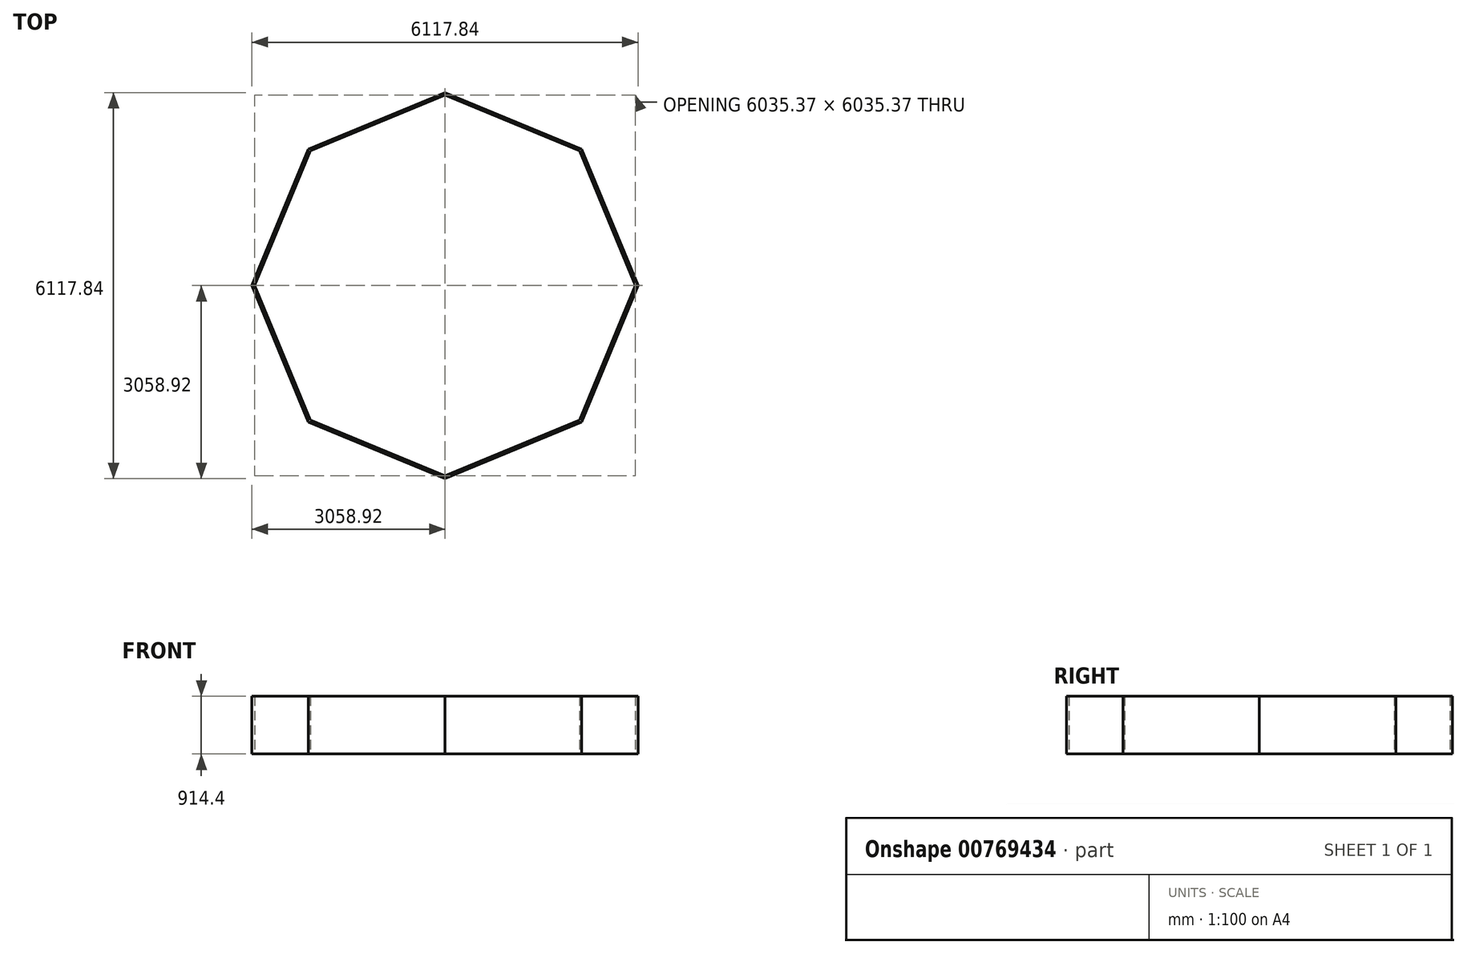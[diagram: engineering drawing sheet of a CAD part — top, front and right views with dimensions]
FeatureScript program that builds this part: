
annotation { "Feature Type Name" : "Feature", "Feature Type Description" : "" }
export const myFeature = defineFeature(function(context is Context, id is Id, definition is map)
    precondition{}
    {
        {
            var Q0;
            Q0=qCreatedBy(makeId("Top.planeOp"),FACE);
            var sketch = newSketch(context, id + "F0", { "sketchPlane" : qUnion([Q0])});
            skCircle(sketch, "E0.cCircle", {"center": v(0, 0) * mm, "radius": 3058.92 * mm, "construction": true});
            skLineSegment(sketch, "E0.0", {"start": v(3058.92, 0) * mm, "end": v(2162.98, -2162.98) * mm});
            skLineSegment(sketch, "E0.1", {"start": v(2162.98, -2162.98) * mm, "end": v(0, -3058.92) * mm});
            skLineSegment(sketch, "E0.2", {"start": v(0, -3058.92) * mm, "end": v(-2162.98, -2162.98) * mm});
            skLineSegment(sketch, "E0.3", {"start": v(-2162.98, -2162.98) * mm, "end": v(-3058.92, 0) * mm});
            skLineSegment(sketch, "E0.4", {"start": v(-3058.92, 0) * mm, "end": v(-2162.98, 2162.98) * mm});
            skLineSegment(sketch, "E0.5", {"start": v(-2162.98, 2162.98) * mm, "end": v(0, 3058.92) * mm});
            skLineSegment(sketch, "E0.6", {"start": v(0, 3058.92) * mm, "end": v(2162.98, 2162.98) * mm});
            skLineSegment(sketch, "E0.7", {"start": v(2162.98, 2162.98) * mm, "end": v(3058.92, 0) * mm});
            skLineSegment(sketch, "E1.0", {"start": v(-3017.68, 0) * mm, "end": v(-2133.82, 2133.82) * mm});
            skLineSegment(sketch, "E1.1", {"start": v(-2133.82, -2133.82) * mm, "end": v(-3017.68, 0) * mm});
            skLineSegment(sketch, "E1.2", {"start": v(-2133.82, 2133.82) * mm, "end": v(0, 3017.68) * mm});
            skLineSegment(sketch, "E1.3", {"start": v(0, -3017.68) * mm, "end": v(-2133.82, -2133.82) * mm});
            skLineSegment(sketch, "E1.4", {"start": v(0, 3017.68) * mm, "end": v(2133.82, 2133.82) * mm});
            skLineSegment(sketch, "E1.5", {"start": v(2133.82, 2133.82) * mm, "end": v(3017.68, 0) * mm});
            skLineSegment(sketch, "E1.6", {"start": v(3017.68, 0) * mm, "end": v(2133.82, -2133.82) * mm});
            skLineSegment(sketch, "E1.7", {"start": v(2133.82, -2133.82) * mm, "end": v(0, -3017.68) * mm});
            skLineSegment(sketch, "E2", {"start": v(0, 3058.92) * mm, "end": v(0, 3017.68) * mm});
            skLineSegment(sketch, "E3", {"start": v(2162.98, 2162.98) * mm, "end": v(2133.82, 2133.82) * mm});
            skLineSegment(sketch, "E4", {"start": v(3017.68, 0) * mm, "end": v(3058.92, 0) * mm});
            skLineSegment(sketch, "E5", {"start": v(2133.82, -2133.82) * mm, "end": v(2162.98, -2162.98) * mm});
            skLineSegment(sketch, "E6", {"start": v(0, -3058.92) * mm, "end": v(0, -3017.68) * mm});
            skLineSegment(sketch, "E7", {"start": v(-2133.82, -2133.82) * mm, "end": v(-2162.98, -2162.98) * mm});
            skLineSegment(sketch, "E8", {"start": v(-3017.68, 0) * mm, "end": v(-3058.92, 0) * mm});
            skLineSegment(sketch, "E9", {"start": v(-2133.82, 2133.82) * mm, "end": v(-2162.98, 2162.98) * mm});
            skSolve(sketch);
        }
        {
            var Q0;
            Q0=makeQuery(id+"F0.imprint","IMPRINT",FACE,{"disambiguationData":[TD([[makeQuery(id+"F0.imprint","IMPRINT",EDGE,{"derivedFrom":sQuery(id+"F0.wireOp",EDGE,"E0.5")}),-1.0]])]});
            var Q1;
            Q1=makeQuery(id+"F0.imprint","IMPRINT",FACE,{"disambiguationData":[TD([[makeQuery(id+"F0.imprint","IMPRINT",EDGE,{"derivedFrom":sQuery(id+"F0.wireOp",EDGE,"E0.6")}),-1.0]])]});
            var Q2;
            Q2=makeQuery(id+"F0.imprint","IMPRINT",FACE,{"disambiguationData":[TD([[makeQuery(id+"F0.imprint","IMPRINT",EDGE,{"derivedFrom":sQuery(id+"F0.wireOp",EDGE,"E0.7")}),-1.0]])]});
            var Q3;
            Q3=makeQuery(id+"F0.imprint","IMPRINT",FACE,{"disambiguationData":[TD([[makeQuery(id+"F0.imprint","IMPRINT",EDGE,{"derivedFrom":sQuery(id+"F0.wireOp",EDGE,"E0.1")}),-1.0]])]});
            var Q4;
            Q4=makeQuery(id+"F0.imprint","IMPRINT",FACE,{"disambiguationData":[TD([[makeQuery(id+"F0.imprint","IMPRINT",EDGE,{"derivedFrom":sQuery(id+"F0.wireOp",EDGE,"E0.0")}),-1.0]])]});
            var Q5;
            Q5=makeQuery(id+"F0.imprint","IMPRINT",FACE,{"disambiguationData":[TD([[makeQuery(id+"F0.imprint","IMPRINT",EDGE,{"derivedFrom":sQuery(id+"F0.wireOp",EDGE,"E0.2")}),-1.0]])]});
            var Q6;
            Q6=makeQuery(id+"F0.imprint","IMPRINT",FACE,{"disambiguationData":[TD([[makeQuery(id+"F0.imprint","IMPRINT",EDGE,{"derivedFrom":sQuery(id+"F0.wireOp",EDGE,"E0.3")}),-1.0]])]});
            var Q7;
            Q7=makeQuery(id+"F0.imprint","IMPRINT",FACE,{"disambiguationData":[TD([[makeQuery(id+"F0.imprint","IMPRINT",EDGE,{"derivedFrom":sQuery(id+"F0.wireOp",EDGE,"E0.4")}),-1.0]])]});
            extrude(context, id + "F1", {"entities" : qUnion([Q0, Q1, Q2, Q3, Q4, Q5, Q6, Q7]), "depth" : 914.4 * mm, "offsetDistance" : 25.4 * mm});
        }
    });
